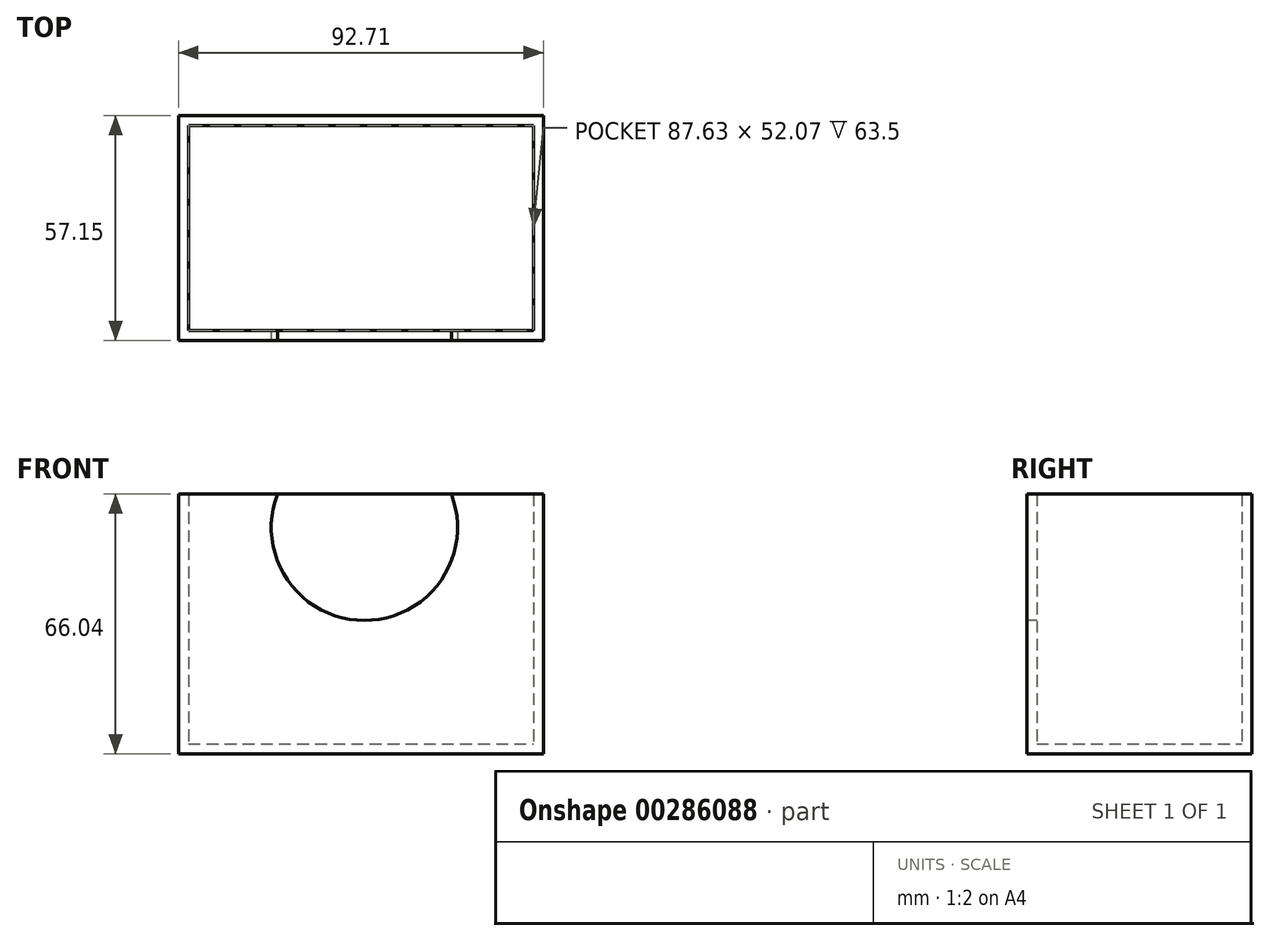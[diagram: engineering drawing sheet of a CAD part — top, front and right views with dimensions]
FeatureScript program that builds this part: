
annotation { "Feature Type Name" : "Feature", "Feature Type Description" : "" }
export const myFeature = defineFeature(function(context is Context, id is Id, definition is map)
    precondition{}
    {
        {
            var Q0;
            Q0=qCreatedBy(makeId("Top.planeOp"),FACE);
            var sketch = newSketch(context, id + "F0", { "sketchPlane" : qUnion([Q0])});
            skLineSegment(sketch, "E0.bottom", {"start": v(0, 0) * mm, "end": v(92.7, 0) * mm});
            skLineSegment(sketch, "E0.top", {"start": v(0, 57.15) * mm, "end": v(92.7, 57.15) * mm});
            skLineSegment(sketch, "E0.left", {"start": v(0, 0) * mm, "end": v(0, 57.15) * mm});
            skLineSegment(sketch, "E0.right", {"start": v(92.7, 0) * mm, "end": v(92.7, 57.15) * mm});
            skSolve(sketch);
        }
        {
            var Q0;
            Q0=makeQuery(id+"F0.imprint","IMPRINT",FACE,{"disambiguationData":[TD([[makeQuery(id+"F0.imprint","IMPRINT",EDGE,{"derivedFrom":sQuery(id+"F0.wireOp",EDGE,"E0.bottom")}),1.0]])]});
            extrude(context, id + "F1", {"entities" : qUnion([Q0]), "depth" : 66.04 * mm});
        }
        {
            var Q0;
            Q0=makeQuery(id+"F1.opExtrude","CAP_FACE",FACE,{"disambiguationData":[OSD([sQuery(id+"F0.wireOp",EDGE,"E0.bottom"),sQuery(id+"F0.wireOp",EDGE,"E0.top"),sQuery(id+"F0.wireOp",EDGE,"E0.left"),sQuery(id+"F0.wireOp",EDGE,"E0.right")])],"isStart":false});
            shell(context, id + "F2", {"entities" : qUnion([Q0]), "thickness" : 2.54 * mm});
        }
        {
            var Q0;
            Q0=makeQuery(id+"F1.opExtrude","SWEPT_FACE",FACE,{"disambiguationData":[OSD([sQuery(id+"F0.wireOp",EDGE,"E0.bottom")])]});
            var sketch = newSketch(context, id + "F3", { "sketchPlane" : qUnion([Q0])});
            skArc(sketch, "E1", {"start": v(36, 66.04) * mm, "mid": v(46.18, 50.05) * mm, "end": v(56.34, 66.04) * mm});
            skSolve(sketch);
        }
        {
            var Q0;
            {var subQ0=sQuery(id+"F3.wireOp",EDGE,"E1");Q0=makeQuery(id+"F3.imprint","IMPRINT",FACE,{"disambiguationData":[TD([[makeQuery(id+"F3.imprint","IMPRINT",EDGE,{"derivedFrom":subQ0}),1.0]])]});}
            extrude(context, id + "F4", {"entities" : qUnion([Q0]), "operationType" : NewBodyOperationType.REMOVE, "oppositeDirection" : true, "depth" : 25.4 * mm});
        }
        {
            var Q0;
            Q0=makeQuery(id+"F1.opExtrude","SWEPT_FACE",FACE,{"disambiguationData":[OSD([sQuery(id+"F0.wireOp",EDGE,"E0.bottom")])]});
            var sketch = newSketch(context, id + "F5", { "sketchPlane" : qUnion([Q0])});
            skArc(sketch, "E2", {"start": v(25.14, 66.04) * mm, "mid": v(47.23, 33.9) * mm, "end": v(69.32, 66.04) * mm});
            skSolve(sketch);
        }
        {
            var Q0;
            {var subQ0=sQuery(id+"F5.wireOp",EDGE,"E2");Q0=makeQuery(id+"F5.imprint","IMPRINT",FACE,{"disambiguationData":[TD([[makeQuery(id+"F5.imprint","IMPRINT",EDGE,{"derivedFrom":subQ0}),1.0]])]});}
            extrude(context, id + "F6", {"entities" : qUnion([Q0]), "operationType" : NewBodyOperationType.REMOVE, "oppositeDirection" : true, "depth" : 25.4 * mm});
        }
    });
